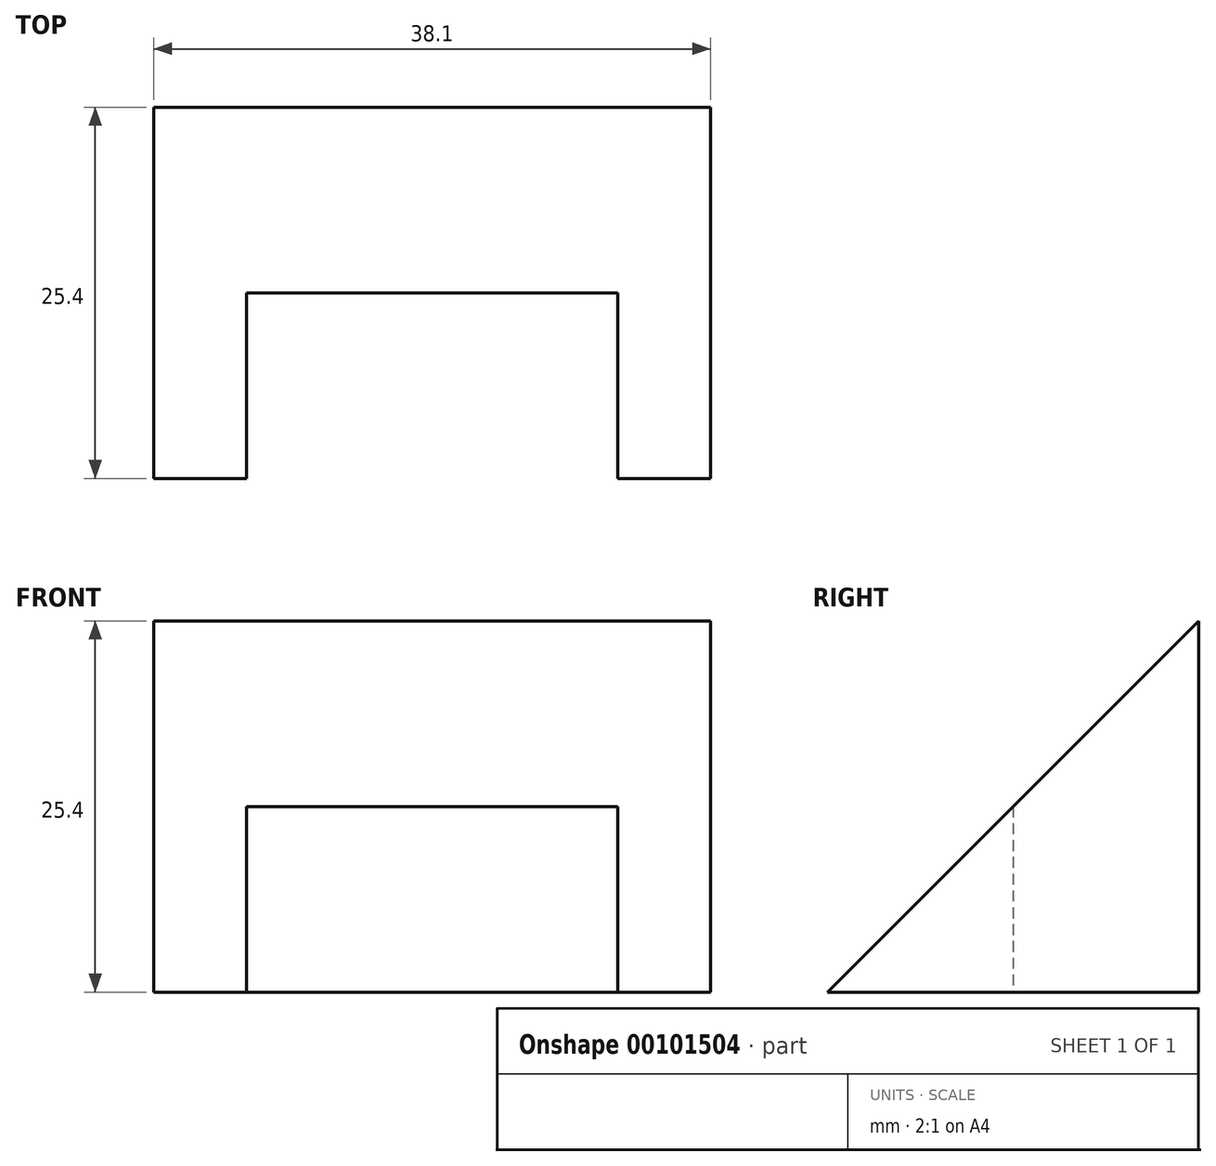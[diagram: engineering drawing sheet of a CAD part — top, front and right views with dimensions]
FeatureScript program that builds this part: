
annotation { "Feature Type Name" : "Feature", "Feature Type Description" : "" }
export const myFeature = defineFeature(function(context is Context, id is Id, definition is map)
    precondition{}
    {
        {
            var Q0;
            Q0=qCreatedBy(makeId("Right.planeOp"),FACE);
            var sketch = newSketch(context, id + "F0", { "sketchPlane" : qUnion([Q0])});
            skLineSegment(sketch, "E0", {"start": v(0, 0) * mm, "end": v(0, 25.4) * mm});
            skLineSegment(sketch, "E1", {"start": v(0, 25.4) * mm, "end": v(-25.4, 0) * mm});
            skLineSegment(sketch, "E2", {"start": v(-25.4, 0) * mm, "end": v(0, 0) * mm});
            skSolve(sketch);
        }
        {
            var Q0;
            Q0 = qSketchRegion(id + "F0", true);
            extrude(context, id + "F1", {"entities" : qUnion([Q0]), "endBound" : BoundingType.SYMMETRIC, "depth" : 38.1 * mm});
        }
        {
            var Q0;
            Q0=qCreatedBy(makeId("Right.planeOp"),FACE);
            var sketch = newSketch(context, id + "F2", { "sketchPlane" : qUnion([Q0])});
            skLineSegment(sketch, "E3", {"start": v(-12.7, 12.7) * mm, "end": v(-12.7, 0) * mm});
            skLineSegment(sketch, "E4", {"start": v(-12.7, 0) * mm, "end": v(-25.4, 0) * mm});
            skLineSegment(sketch, "E5", {"start": v(-25.4, 0) * mm, "end": v(-12.7, 12.7) * mm});
            skSolve(sketch);
        }
        {
            var Q0;
            Q0 = qSketchRegion(id + "F2", true);
            extrude(context, id + "F3", {"entities" : qUnion([Q0]), "operationType" : NewBodyOperationType.REMOVE, "endBound" : BoundingType.SYMMETRIC, "oppositeDirection" : true, "depth" : 25.4 * mm});
        }
    });
